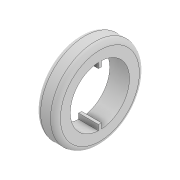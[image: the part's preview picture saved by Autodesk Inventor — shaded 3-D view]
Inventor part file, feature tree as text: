
AUTODESK INVENTOR PART (.ipt)
format: ipt  version: 2022 (Build 260153000, 153)  size: 144,384 bytes
history: native  units: mm
features: thicken_offset x3, extrude x1, fillet x1, sketch x1
ambient origin geometry x8: Origin, YZ Plane, XZ Plane, XY Plane, X Axis, Y Axis, Z Axis, Center Point
bodies: Solid1 (feature_tree)
feature tree (6):
  extrude  "Extrusion1"  Depth=0.5mm
  fillet  "Fillet1"  Radius=2.0mm
  thicken_offset  "Thicken2"
  thicken_offset  "Thicken3"
  thicken_offset  "Thicken4"
  sketch  "Sketch1"  dims[d0=5.7mm d1=9.0mm d2=2.0mm d3=0.0mm d4=0.5mm d5=0.5mm d6=0.5mm d7=0.5mm d10=0.5mm d11=0.1mm d12=0.1mm d13=0.15mm d14=0.15mm d15=0.15mm d16=0.15mm]
